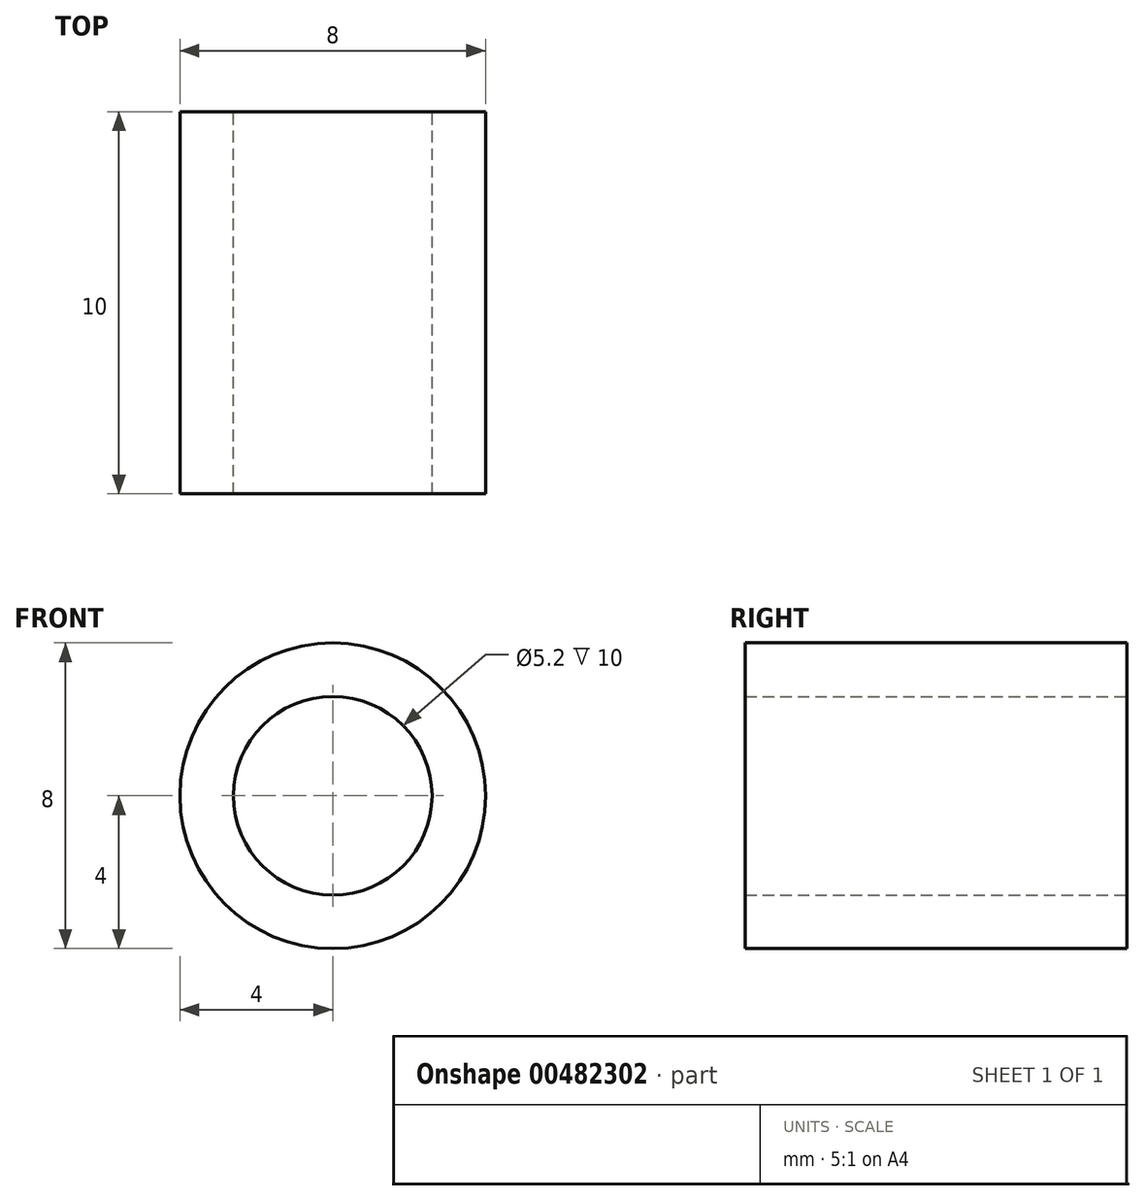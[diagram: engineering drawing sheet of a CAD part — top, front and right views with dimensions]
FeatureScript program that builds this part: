
annotation { "Feature Type Name" : "Feature", "Feature Type Description" : "" }
export const myFeature = defineFeature(function(context is Context, id is Id, definition is map)
    precondition{}
    {
        {
            var Q0;
            Q0=qCreatedBy(makeId("Front.planeOp"),FACE);
            var sketch = newSketch(context, id + "F0", { "sketchPlane" : qUnion([Q0])});
            skCircle(sketch, "E0", {"center": v(0, 0) * mm, "radius": 2.6 * mm});
            skCircle(sketch, "E1", {"center": v(0, 0) * mm, "radius": 4 * mm});
            skSolve(sketch);
        }
        {
            var Q0;
            Q0=makeQuery(id+"F0.imprint","IMPRINT",FACE,{"disambiguationData":[TD([[makeQuery(id+"F0.imprint","IMPRINT",EDGE,{"derivedFrom":sQuery(id+"F0.wireOp",EDGE,"E0")}),-1.0]])]});
            extrude(context, id + "F1", {"entities" : qUnion([Q0]), "depth" : 10 * mm});
        }
    });
